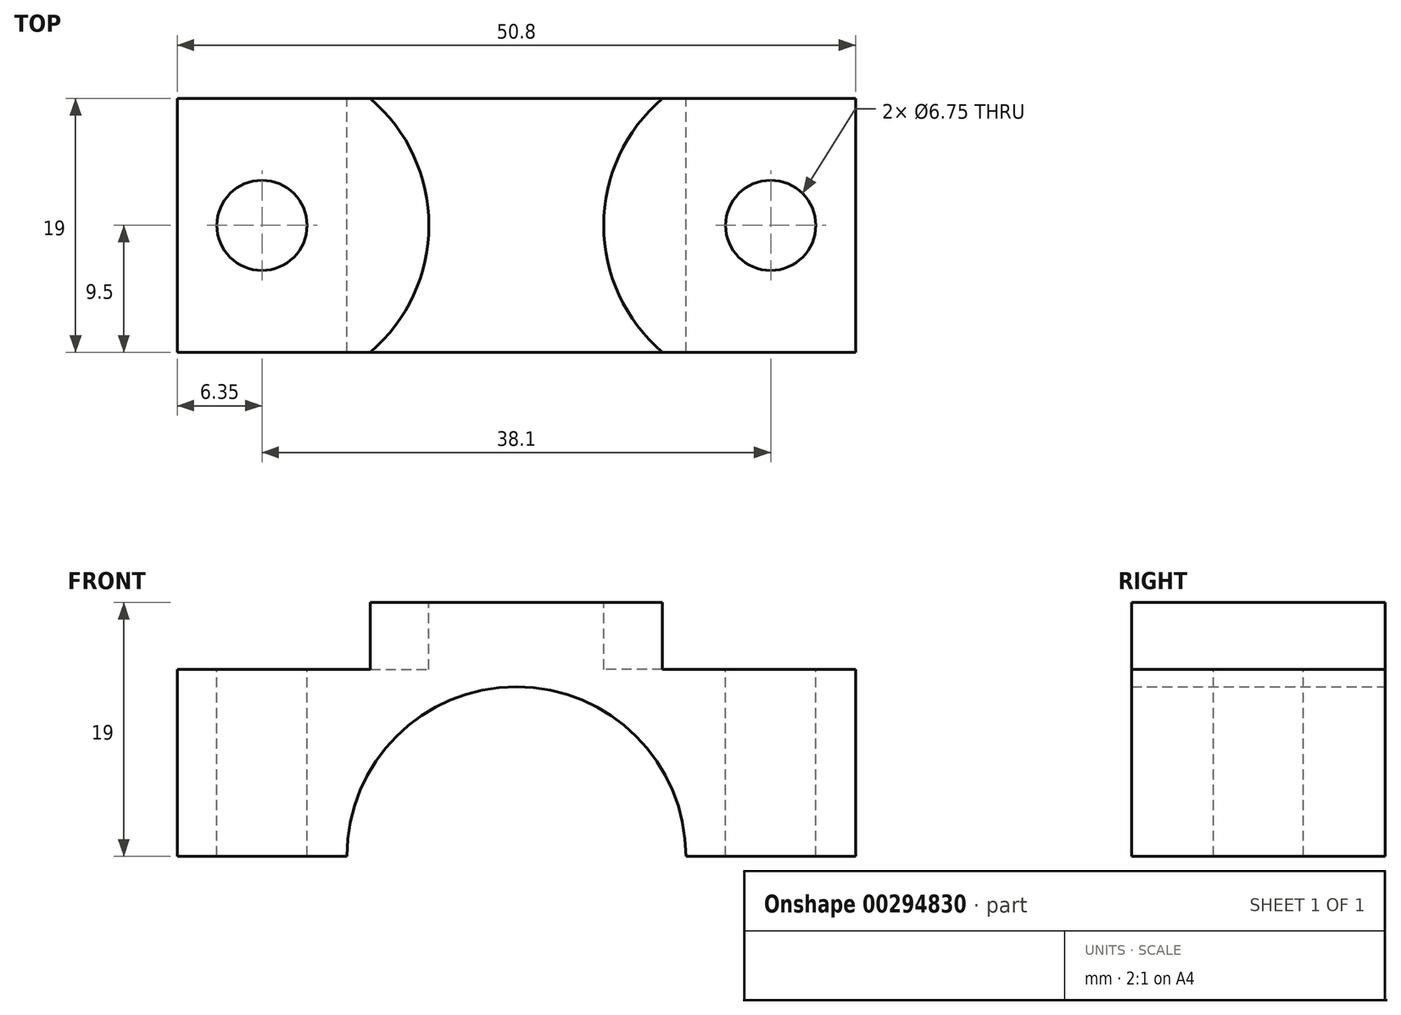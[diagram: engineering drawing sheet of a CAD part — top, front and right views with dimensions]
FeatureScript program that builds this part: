
annotation { "Feature Type Name" : "Feature", "Feature Type Description" : "" }
export const myFeature = defineFeature(function(context is Context, id is Id, definition is map)
    precondition{}
    {
        {
            var Q0;
            Q0=qCreatedBy(makeId("Front.planeOp"),FACE);
            var sketch = newSketch(context, id + "F0", { "sketchPlane" : qUnion([Q0])});
            skLineSegment(sketch, "E0.bottom", {"start": v(-25.4, 0) * mm, "end": v(25.4, 0) * mm});
            skLineSegment(sketch, "E0.top", {"start": v(-25.4, 19) * mm, "end": v(25.4, 19) * mm});
            skLineSegment(sketch, "E0.left", {"start": v(-25.4, 0) * mm, "end": v(-25.4, 19) * mm});
            skLineSegment(sketch, "E0.right", {"start": v(25.4, 0) * mm, "end": v(25.4, 19) * mm});
            skCircle(sketch, "E1", {"center": v(0, 0) * mm, "radius": 12.7 * mm});
            skSolve(sketch);
        }
        {
            var Q0;
            Q0=makeQuery(id+"F0.imprint","IMPRINT",FACE,{"disambiguationData":[TD([[makeQuery(id+"F0.imprint","IMPRINT",EDGE,{"derivedFrom":sQuery(id+"F0.wireOp",EDGE,"E0.top")}),-1.0]])]});
            extrude(context, id + "F1", {"entities" : qUnion([Q0]), "endBound" : BoundingType.SYMMETRIC, "depth" : 19 * mm});
        }
        {
            var Q0;
            {var subQ0=sQuery(id+"F0.wireOp",EDGE,"E0.bottom");Q0=makeQuery(id+"F1.opExtrude","SWEPT_FACE",FACE,{"disambiguationData":[OSD([subQ0]),TDD([makeQuery(id+"F0.imprint","IMPRINT",EDGE,{"disambiguationData":[TD([[makeQuery(id+"F0.imprint","INTERSECT",VERTEX,{"derivedFrom":[subQ0,sQuery(id+"F0.wireOp",EDGE,"E0.left")]}),-1.0]])],"derivedFrom":subQ0})])]});}
            var sketch = newSketch(context, id + "F2", { "sketchPlane" : qUnion([Q0])});
            skLineSegment(sketch, "E2", {"start": v(-25.4, 0) * mm, "end": v(-12.7, 0) * mm, "construction": true});
            skLineSegment(sketch, "E3", {"start": v(25.4, 0) * mm, "end": v(12.7, 0) * mm, "construction": true});
            skPoint(sketch, "E4", {"position": v(-19.05, 0) * mm});
            skPoint(sketch, "E5", {"position": v(19.05, 0) * mm});
            skSolve(sketch);
        }
        {
            var Q0;
            Q0=makeQuery(id+"F1.opExtrude","SWEPT_FACE",FACE,{"disambiguationData":[OSD([sQuery(id+"F0.wireOp",EDGE,"E0.top")])]});
            var sketch = newSketch(context, id + "F3", { "sketchPlane" : qUnion([Q0])});
            skPoint(sketch, "E6.0", {"position": v(-19.05, 0) * mm});
            skPoint(sketch, "E7.0", {"position": v(19.05, 0) * mm});
            skSolve(sketch);
        }
        {
            var Q0;
            Q0=sQuery(id+"F3.wireOp",VERTEX,"E7.0");
            var Q1;
            Q1=sQuery(id+"F3.wireOp",VERTEX,"E6.0");
            var Q2;
            Q2=makeQuery(id+"F1.opExtrude","SWEPT_BODY",BODY,{"disambiguationData":[OSD([sQuery(id+"F0.wireOp",EDGE,"E0.bottom"),sQuery(id+"F0.wireOp",EDGE,"E0.top"),sQuery(id+"F0.wireOp",EDGE,"E0.left"),sQuery(id+"F0.wireOp",EDGE,"E0.right"),sQuery(id+"F0.wireOp",EDGE,"E1")])]});
            hole(context, id + "F4", {"style" : HoleStyle.C_BORE, "holeDiameter" : 6.75 * mm, "cBoreDiameter" : 25 * mm, "cBoreDepth" : 5 * mm, "endStyle" : HoleEndStyle.THROUGH, "locations" : qUnion([Q0, Q1]), "scope" : qUnion([Q2])});
        }
    });
